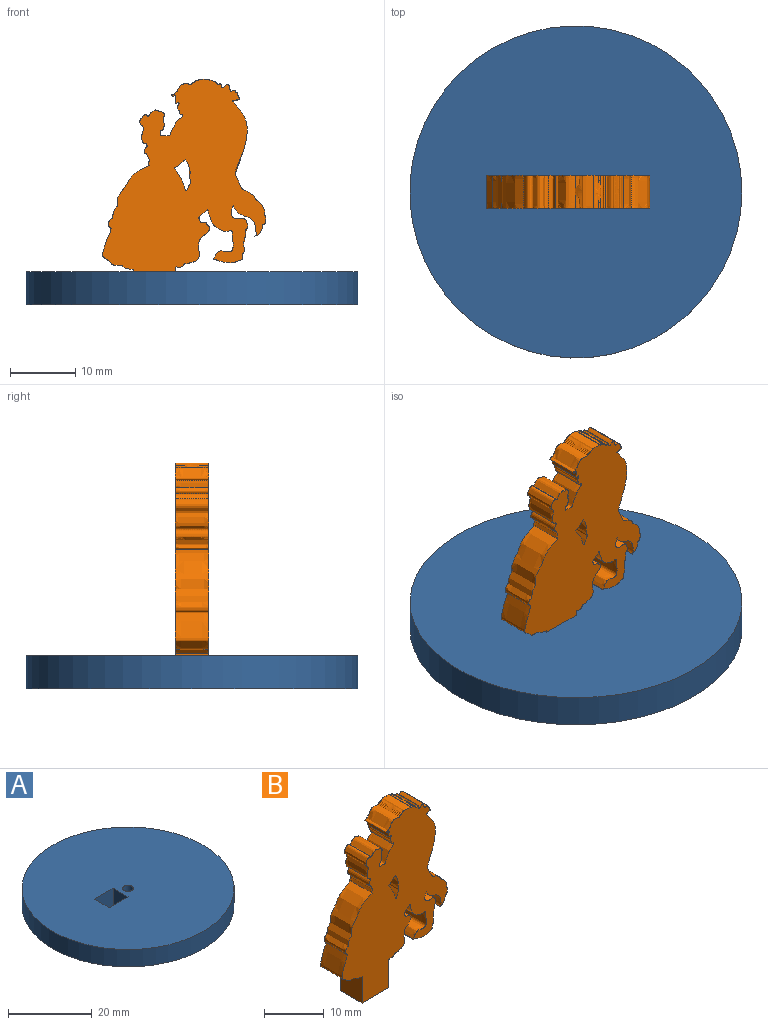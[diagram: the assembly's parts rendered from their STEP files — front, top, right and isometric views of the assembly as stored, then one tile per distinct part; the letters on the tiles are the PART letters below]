
ASSEMBLY  parts=2 mates=1
PART A: 8 faces, bbox 50.8x50.8x5.1 mm
  f0: plane 6.35x5.08mm, normal (0,-1,0), area 32.3mm2, adj f1,f5,f6,f7
  f1: plane 5.08x5.08mm, normal (-1,0,0), area 25.8mm2, adj f0,f2,f6,f7
  f2: plane 6.35x5.08mm, normal (0,1,0), area 32.3mm2, adj f1,f5,f6,f7
  f3: cylinder r=25.4mm len=50.8mm, axis (0,0,-1), area 810.7mm2, adj f6,f7
  f4: cylinder r=1.27mm len=5.08mm, axis (0,0,-1), area 40.5mm2, adj f6,f7
  f5: plane 5.08x5.08mm, normal (1,0,0), area 25.8mm2, adj f0,f2,f6,f7
  f6: plane 50.8x50.8mm, normal (0,0,1), area 1989.5mm2, adj f0,f1,f2,f3,f4,f5
  f7: plane 50.8x50.8mm, normal (0,0,-1), area 1989.5mm2, adj f0,f1,f2,f3,f4,f5
PART B: 14 faces, bbox 25x5.1x34.6 mm
  f0: extruded ~15.93x7.13mm, area 112.7mm2, adj f3,f9,f10,f11
  f1: extruded ~5.08x4.65mm, area 45.5mm2, adj f8,f9,f10
  f2: extruded ~6.2x5.08mm, area 46.2mm2, adj f3,f7,f9,f10
  f3: extruded ~8.39x5.08mm, area 87mm2, adj f0,f2,f9,f10
  f4: extruded ~8.76x5.26mm, area 72.4mm2, adj f5,f9,f10,f12
  f5: extruded ~8.8x6.14mm, area 134.9mm2, adj f4,f6,f9,f10
  f6: extruded ~5.08x4.78mm, area 33.2mm2, adj f5,f7,f9,f10
  f7: extruded ~24.06x14.45mm, area 226.7mm2, adj f2,f6,f9,f10
  f8: extruded ~5.08x1.75mm, area 10.9mm2, adj f1,f9,f10
  f9: plane 34.58x25.04mm, normal (0,-1,0), area 475mm2, adj f0,f1,f2,f3,f4,f5,f6,f7
  f10: plane 34.58x25.04mm, normal (0,1,0), area 475mm2, adj f0,f1,f2,f3,f4,f5,f6,f7
  f11: plane 5.42x5.08mm, normal (-1,0,0), area 27.5mm2, adj f0,f9,f10,f13
  f12: plane 5.78x5.08mm, normal (1,0,0), area 29.4mm2, adj f4,f9,f10,f13
  f13: plane 6.35x5.08mm, normal (0,0,-1), area 32.3mm2, adj f9,f10,f11,f12
PLACE A at identity fixed
PLACE B t=(0.64,2.54,5.08)mm
MATE fastened B.f13 <-> A.f7  axis (0,0,-1) through (-5.72,0,0)mm
